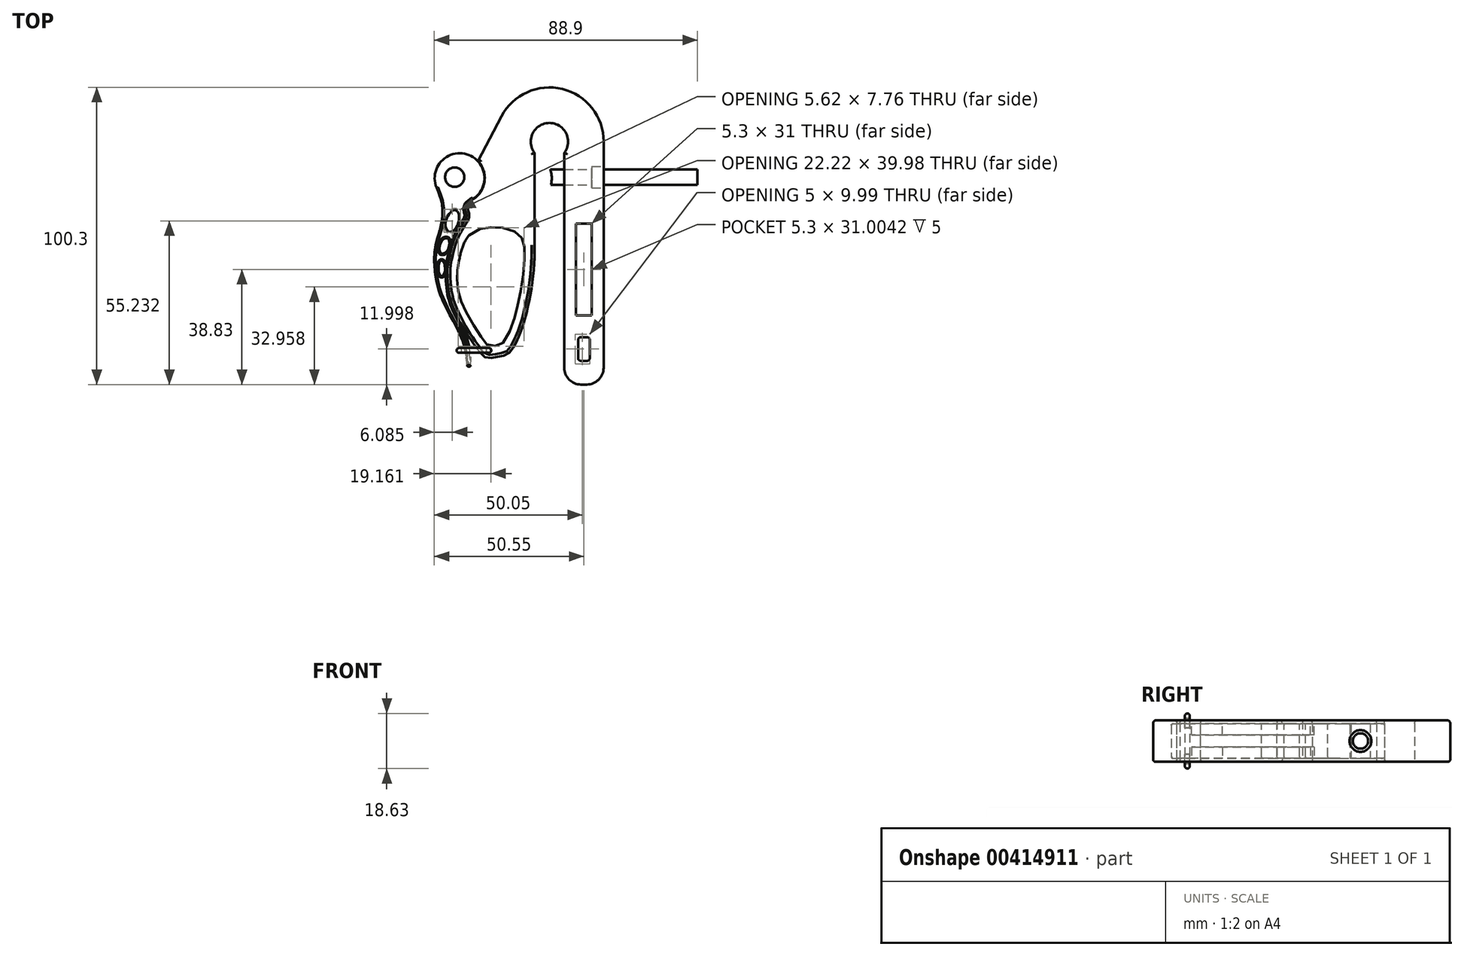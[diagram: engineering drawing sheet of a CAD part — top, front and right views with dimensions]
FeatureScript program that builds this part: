
annotation { "Feature Type Name" : "Feature", "Feature Type Description" : "" }
export const myFeature = defineFeature(function(context is Context, id is Id, definition is map)
    precondition{}
    {
        {
            var Q0;
            Q0=qCreatedBy(makeId("Top.planeOp"),FACE);
            var sketch = newSketch(context, id + "F0", { "sketchPlane" : qUnion([Q0])});
            skLineSegment(sketch, "E0", {"start": v(4.25, 15.7) * mm, "end": v(14.25, 15.7) * mm});
            skSolve(sketch);
        }
        {
            var Q0;
            Q0=qCreatedBy(makeId("Top.planeOp"),FACE);
            var sketch = newSketch(context, id + "F1", { "sketchPlane" : qUnion([Q0])});
            skCircle(sketch, "E1", {"center": v(-9.26, -5.46) * mm, "radius": 3.25 * mm});
            skSolve(sketch);
        }
        {
            var Q0;
            Q0=qCreatedBy(makeId("Top.planeOp"),FACE);
            var sketch = newSketch(context, id + "F2", { "sketchPlane" : qUnion([Q0])});
            skLineSegment(sketch, "E2", {"start": v(-10.3, -5.78) * mm, "end": v(52.53, -5.78) * mm});
            skCircle(sketch, "E3", {"center": v(-7.6, -5.78) * mm, "radius": 8.4 * mm});
            skFitSpline(sketch, "E4", {"points": [v(-15.34, -9.05) * mm, v(-13.72, -13.54) * mm, v(-13.38, -15.5) * mm, v(-13.36, -18.35) * mm, v(-14.1, -22.73) * mm, v(-15.23, -26.6) * mm, v(-15.74, -28.68) * mm, v(-16.08, -31.46) * mm, v(-16.14, -34.4) * mm, v(-15.88, -37.64) * mm, v(-15.5, -39.95) * mm, v(-14.68, -43.49) * mm, v(-13.78, -45.98) * mm, v(-10.97, -51.82) * mm, v(-8.53, -56.37) * mm, v(-7.1, -59.45) * mm, v(-6.08, -62.54) * mm, v(-5.33, -66.95) * mm, v(-5.19, -67.88) * mm, v(-5.05, -69.1) * mm, v(-4.96, -69.3) * mm, v(-4.77, -69.34) * mm, v(-4.09, -69.33) * mm, v(-3.77, -69.02) * mm, v(-3.6, -68.48) * mm, v(-3.65, -67.26) * mm, v(-3.98, -64.6) * mm, v(-4.65, -61.42) * mm, v(-5, -60.18) * mm, v(-5.89, -57.85) * mm, v(-6.72, -56) * mm, v(-8.46, -52.48) * mm, v(-9.55, -50.16) * mm, v(-10.27, -48.37) * mm, v(-10.98, -45.85) * mm, v(-11.43, -43.59) * mm, v(-11.72, -40.7) * mm, v(-11.83, -37.94) * mm, v(-11.8, -36.87) * mm, v(-11.65, -35.17) * mm, v(-11.43, -33.62) * mm, v(-11.1, -32.1) * mm, v(-10.18, -28.54) * mm, v(-9.68, -27) * mm, v(-8.1, -23.55) * mm, v(-6.99, -21.67) * mm, v(-5.8, -19.74) * mm, v(-5.58, -19.3) * mm, v(-5.45, -18.9) * mm, v(-5.4, -18.5) * mm, v(-5.41, -18.12) * mm, v(-5.54, -17.64) * mm, v(-5.72, -17.08) * mm, v(-5.82, -16.42) * mm, v(-5.73, -15.64) * mm, v(-5.6, -15.24) * mm, v(-5.17, -14.43) * mm, v(-4.56, -13.85) * mm, v(-3, -12.81) * mm], "startDerivative": vector(70.6, -181.98) * mm, "endDerivative": vector(100.87, 65.97) * mm});
            skFitSpline(sketch, "E5", {"points": [v(-12.38, -21.6) * mm, v(-12.3, -20.68) * mm, v(-11.9, -19.22) * mm, v(-10.97, -17.7) * mm, v(-10.2, -16.9) * mm, v(-9.44, -16.54) * mm, v(-8.67, -16.63) * mm, v(-8.14, -17.3) * mm, v(-7.79, -18.55) * mm, v(-7.83, -20.2) * mm, v(-8.38, -21.96) * mm, v(-9.3, -23.15) * mm, v(-10.26, -23.86) * mm, v(-10.94, -24) * mm, v(-11.3, -23.86) * mm, v(-11.8, -23.39) * mm, v(-12.2, -22.56) * mm, v(-12.38, -21.6) * mm]});
            skFitSpline(sketch, "E6", {"points": [v(-14.34, -28.7) * mm, v(-14.12, -27.96) * mm, v(-13.63, -27.02) * mm, v(-12.98, -26.32) * mm, v(-12.3, -26.07) * mm, v(-11.62, -26.18) * mm, v(-11.23, -26.62) * mm, v(-11.03, -27.4) * mm, v(-11.15, -28.57) * mm, v(-11.63, -29.94) * mm, v(-12.2, -30.69) * mm, v(-12.9, -31.17) * mm, v(-13.48, -31.26) * mm, v(-13.94, -31.1) * mm, v(-14.28, -30.5) * mm, v(-14.41, -29.7) * mm, v(-14.34, -28.7) * mm]});
            skFitSpline(sketch, "E7", {"points": [v(-14.7, -35.72) * mm, v(-14.54, -34.72) * mm, v(-14.3, -34.12) * mm, v(-13.97, -33.72) * mm, v(-13.5, -33.64) * mm, v(-13.16, -33.88) * mm, v(-12.84, -34.4) * mm, v(-12.6, -35.26) * mm, v(-12.54, -36.12) * mm, v(-12.54, -36.9) * mm, v(-12.72, -37.72) * mm, v(-13.03, -38.4) * mm, v(-13.3, -38.74) * mm, v(-13.7, -38.85) * mm, v(-14.12, -38.56) * mm, v(-14.5, -37.72) * mm, v(-14.68, -36.96) * mm, v(-14.7, -35.72) * mm]});
            skSolve(sketch);
        }
        {
            var Q0;
            {var subQ0=sQuery(id+"F2.wireOp",EDGE,"E4");Q0=makeQuery(id+"F2.imprint","IMPRINT",FACE,{"disambiguationData":[TD([[makeQuery(id+"F2.imprint","IMPRINT",EDGE,{"derivedFrom":subQ0}),1.0]])]});}
            var Q1;
            {var subQ0=sQuery(id+"F2.wireOp",EDGE,"E4");var subQ1=sQuery(id+"F2.wireOp",EDGE,"E3");var subQ2=makeQuery(id+"F2.imprint","INTERSECT",VERTEX,{"disambiguationData":[OD(0.0)],"derivedFrom":[subQ1,subQ0]});Q1=makeQuery(id+"F2.imprint","IMPRINT",FACE,{"disambiguationData":[TD([[makeQuery(id+"F2.imprint","IMPRINT",EDGE,{"disambiguationData":[TD([[subQ2,1.0]])],"derivedFrom":subQ1}),1.0]])]});}
            extrude(context, id + "F3", {"entities" : qUnion([Q0, Q1]), "depth" : 11.64 * mm});
        }
        {
            var Q0;
            Q0=qCreatedBy(makeId("Top.planeOp"),FACE);
            var sketch = newSketch(context, id + "F4", { "sketchPlane" : qUnion([Q0])});
            skCircle(sketch, "E8", {"center": v(-9.26, -5.46) * mm, "radius": 3.25 * mm});
            skSolve(sketch);
        }
        {
            var Q0;
            Q0=makeQuery(id+"F1.imprint","IMPRINT",FACE,{"disambiguationData":[TD([[makeQuery(id+"F1.imprint","IMPRINT",EDGE,{"derivedFrom":sQuery(id+"F1.wireOp",EDGE,"E1")}),1.0]])]});
            extrude(context, id + "F5", {"entities" : qUnion([Q0]), "operationType" : NewBodyOperationType.REMOVE, "endBound" : BoundingType.THROUGH_ALL, "depth" : 25 * mm});
        }
        {
            var Q0;
            Q0=makeQuery(id+"F3.opExtrude","CAP_EDGE",EDGE,{"disambiguationData":[OSD([sQuery(id+"F2.wireOp",EDGE,"E4")])],"isStart":false});
            var Q1;
            Q1=makeQuery(id+"F3.opExtrude","CAP_EDGE",EDGE,{"disambiguationData":[OSD([sQuery(id+"F2.wireOp",EDGE,"E3")])],"isStart":false});
            var Q2;
            Q2=makeQuery(id+"F3.opExtrude","CAP_EDGE",EDGE,{"disambiguationData":[OSD([sQuery(id+"F2.wireOp",EDGE,"E5")])],"isStart":false});
            var Q3;
            Q3=makeQuery(id+"F3.opExtrude","CAP_EDGE",EDGE,{"disambiguationData":[OSD([sQuery(id+"F2.wireOp",EDGE,"E6")])],"isStart":false});
            var Q4;
            Q4=makeQuery(id+"F3.opExtrude","CAP_EDGE",EDGE,{"disambiguationData":[OSD([sQuery(id+"F2.wireOp",EDGE,"E7")])],"isStart":false});
            var Q5;
            Q5=makeQuery(id+"F3.opExtrude","CAP_EDGE",EDGE,{"disambiguationData":[OSD([sQuery(id+"F2.wireOp",EDGE,"E4")])],"isStart":true});
            var Q6;
            Q6=makeQuery(id+"F3.opExtrude","CAP_EDGE",EDGE,{"disambiguationData":[OSD([sQuery(id+"F2.wireOp",EDGE,"E6")])],"isStart":true});
            var Q7;
            Q7=makeQuery(id+"F3.opExtrude","CAP_EDGE",EDGE,{"disambiguationData":[OSD([sQuery(id+"F2.wireOp",EDGE,"E5")])],"isStart":true});
            var Q8;
            Q8=makeQuery(id+"F3.opExtrude","CAP_EDGE",EDGE,{"disambiguationData":[OSD([sQuery(id+"F2.wireOp",EDGE,"E7")])],"isStart":true});
            fillet(context, id + "F6", {"entities" : qUnion([Q0, Q1, Q2, Q3, Q4, Q5, Q6, Q7, Q8]), "radius" : 0.5 * mm, "tangentPropagation" : true, "allowEdgeOverflow" : false});
        }
        {
            var Q0;
            Q0=qCreatedBy(makeId("Top.planeOp"),FACE);
            cPlane(context, id + "F7", {"entities" : qUnion([Q0]), "cplaneType" : CPlaneType.OFFSET, "offset" : 5.83 * mm, "width" : 150 * mm, "height" : 150 * mm});
        }
        {
            var Q0;
            Q0=qCreatedBy(id+"F7.planeOp",FACE);
            var sketch = newSketch(context, id + "F8", { "sketchPlane" : qUnion([Q0])});
            skLineSegment(sketch, "E9", {"start": v(0.79, -5.46) * mm, "end": v(40, -5.46) * mm});
            skLineSegment(sketch, "E10", {"start": v(-9.26, -5.46) * mm, "end": v(10.7, -5.46) * mm, "construction": true});
            skSolve(sketch);
        }
        {
            var Q0;
            Q0=qCreatedBy(makeId("Right.planeOp"),FACE);
            cPlane(context, id + "F9", {"entities" : qUnion([Q0]), "cplaneType" : CPlaneType.OFFSET, "offset" : 50 * mm, "width" : 150 * mm, "height" : 150 * mm});
        }
        {
            var Q0;
            Q0=qCreatedBy(id+"F9.planeOp",FACE);
            var sketch = newSketch(context, id + "F10", { "sketchPlane" : qUnion([Q0])});
            skCircle(sketch, "E11", {"center": v(-5.46, 5.83) * mm, "radius": 2.6 * mm});
            skSolve(sketch);
        }
        {
            var Q0;
            Q0=qSketchRegion(id+"F10",true);
            extrude(context, id + "F11", {"entities" : qUnion([Q0]), "endBound" : BoundingType.UP_TO_NEXT, "oppositeDirection" : true, "depth" : 25 * mm});
        }
        {
            var Q0;
            Q0=makeQuery(id+"F3.opExtrude","SWEPT_BODY",BODY,{"disambiguationData":[OSD([sQuery(id+"F2.wireOp",EDGE,"E3"),sQuery(id+"F2.wireOp",EDGE,"E4"),sQuery(id+"F2.wireOp",EDGE,"E5"),sQuery(id+"F2.wireOp",EDGE,"E6"),sQuery(id+"F2.wireOp",EDGE,"E7")])]});
            var Q1;
            Q1=qCreatedBy(makeId("Right.planeOp"),FACE);
            transform(context, id + "F12", {"entities" : qUnion([Q0]), "transformType" : TransformType.TRANSLATION_DISTANCE, "transformDirection" : qUnion([Q1]), "distance" : 22.75 * mm, "oppositeDirection" : true, "makeCopy" : false});
        }
        {
            var Q0;
            Q0=qCreatedBy(id+"F7.planeOp",FACE);
            var sketch = newSketch(context, id + "F13", { "sketchPlane" : qUnion([Q0])});
            skCircle(sketch, "E12", {"center": v(0, 6.54) * mm, "radius": 6.3 * mm, "construction": true});
            skArc(sketch, "E13", {"start": v(-18.3, 6.54) * mm, "mid": v(0, 24.84) * mm, "end": v(18.3, 6.54) * mm, "construction": true});
            skLineSegment(sketch, "E14", {"start": v(-5, 2.7) * mm, "end": v(-5, -75.46) * mm, "construction": true});
            skLineSegment(sketch, "E15.MirrorCS", {"start": v(5, 2.7) * mm, "end": v(5, -75.46) * mm, "construction": true});
            skLineSegment(sketch, "E16", {"start": v(18.3, 6.54) * mm, "end": v(18.3, -75.46) * mm, "construction": true});
            skLineSegment(sketch, "E17", {"start": v(-24.12, 0) * mm, "end": v(-16.2, 15.06) * mm, "construction": true});
            skArc(sketch, "E18.0", {"start": v(-24.12, 0) * mm, "mid": v(-21.95, -7.05) * mm, "end": v(-26.11, -13.15) * mm, "construction": true});
            skFitSpline(sketch, "E19.0", {"points": [v(-25.7, -12.88) * mm, v(-25.84, -12.97) * mm, v(-26.1, -13.15) * mm, v(-26.5, -13.4) * mm, v(-26.9, -13.67) * mm, v(-27.3, -13.94) * mm, v(-27.6, -14.19) * mm, v(-27.8, -14.42) * mm, v(-27.97, -14.67) * mm, v(-28.12, -14.95) * mm, v(-28.24, -15.24) * mm, v(-28.33, -15.45) * mm, v(-28.4, -15.67) * mm, v(-28.45, -15.97) * mm, v(-28.49, -16.36) * mm, v(-28.45, -16.8) * mm, v(-28.34, -17.18) * mm, v(-28.25, -17.48) * mm, v(-28.17, -17.7) * mm, v(-28.1, -17.94) * mm, v(-28.06, -18.2) * mm, v(-28.06, -18.44) * mm, v(-28.07, -18.68) * mm, v(-28.1, -18.94) * mm, v(-28.18, -19.18) * mm, v(-28.28, -19.4) * mm, v(-28.38, -19.63) * mm, v(-28.5, -19.84) * mm, v(-28.74, -20.25) * mm, v(-29.12, -20.86) * mm, v(-29.63, -21.67) * mm, v(-30.15, -22.48) * mm, v(-30.63, -23.3) * mm, v(-31.05, -24.13) * mm, v(-31.45, -24.98) * mm, v(-31.84, -25.84) * mm, v(-32.2, -26.7) * mm, v(-32.56, -27.57) * mm, v(-32.82, -28.47) * mm, v(-33.07, -29.4) * mm, v(-33.3, -30.31) * mm, v(-33.54, -31.23) * mm, v(-33.77, -32.16) * mm, v(-34, -33.08) * mm, v(-34.16, -34) * mm, v(-34.29, -34.92) * mm, v(-34.38, -35.85) * mm, v(-34.44, -36.63) * mm, v(-34.48, -37.25) * mm, v(-34.5, -37.87) * mm, v(-34.48, -38.65) * mm, v(-34.44, -39.59) * mm, v(-34.4, -40.53) * mm, v(-34.32, -41.47) * mm, v(-34.21, -42.73) * mm, v(-34, -44.28) * mm, v(-33.66, -45.79) * mm, v(-33.35, -46.98) * mm, v(-33.09, -47.87) * mm, v(-32.8, -48.75) * mm, v(-32.44, -49.61) * mm, v(-32.06, -50.47) * mm, v(-31.67, -51.32) * mm, v(-31.26, -52.17) * mm, v(-30.84, -53.01) * mm, v(-30.43, -53.85) * mm, v(-30, -54.7) * mm, v(-29.59, -55.54) * mm, v(-29.17, -56.4) * mm, v(-28.78, -57.25) * mm, v(-28.42, -58.13) * mm, v(-28.08, -59) * mm, v(-27.8, -59.74) * mm, v(-27.6, -60.34) * mm, v(-27.46, -60.8) * mm, v(-27.34, -61.25) * mm, v(-27.2, -61.87) * mm, v(-27.02, -62.64) * mm, v(-26.82, -63.56) * mm, v(-26.64, -64.5) * mm, v(-26.5, -65.43) * mm, v(-26.41, -66.22) * mm, v(-26.35, -66.84) * mm, v(-26.3, -67.31) * mm, v(-26.26, -67.7) * mm, v(-26.24, -68.02) * mm, v(-26.23, -68.27) * mm, v(-26.25, -68.51) * mm, v(-26.3, -68.76) * mm, v(-26.4, -69) * mm, v(-26.48, -69.14) * mm, v(-26.54, -69.21) * mm], "construction": true});
            skFitSpline(sketch, "E20", {"points": [v(-29.53, -55.65) * mm, v(-24.4, -63.35) * mm, v(-21.24, -66.37) * mm, v(-16.84, -65.96) * mm, v(-13.48, -64.6) * mm, v(-5.01, -28.32) * mm], "startDerivative": vector(26.21, -45.22) * mm, "endDerivative": vector(-2.06, 128.2) * mm, "construction": true});
            skLineSegment(sketch, "E21", {"start": v(5, -75.46) * mm, "end": v(18.3, -75.46) * mm, "construction": true});
            skFitSpline(sketch, "E22", {"points": [v(-30.52, -33.64) * mm, v(-27.1, -25.02) * mm], "startDerivative": vector(2.2, 9.83) * mm, "endDerivative": vector(6.97, 8.55) * mm});
            skFitSpline(sketch, "E23", {"points": [v(-29.66, -21.72) * mm, v(-31.4, -24.89) * mm, v(-32.64, -27.88) * mm, v(-33.72, -31.93) * mm], "startDerivative": vector(-6, -10.28) * mm, "endDerivative": vector(-2.9, -11.97) * mm});
            skLineSegment(sketch, "E24", {"start": v(-16.2, 15.06) * mm, "end": v(-24.12, 0) * mm});
            skArc(sketch, "E25", {"start": v(-16.2, 15.06) * mm, "mid": v(4.39, 24.3) * mm, "end": v(18.3, 6.54) * mm});
            skLineSegment(sketch, "E26", {"start": v(18.3, -75.46) * mm, "end": v(18.3, 6.54) * mm});
            skLineSegment(sketch, "E27", {"start": v(18.3, -75.46) * mm, "end": v(5, -75.46) * mm});
            skLineSegment(sketch, "E28", {"start": v(5, 2.7) * mm, "end": v(5, -75.46) * mm});
            skArc(sketch, "E29", {"start": v(5, 2.7) * mm, "mid": v(0, 12.84) * mm, "end": v(-5, 2.7) * mm});
            skLineSegment(sketch, "E30", {"start": v(-5, -28.36) * mm, "end": v(-5, 2.7) * mm});
            skArc(sketch, "E31", {"start": v(-24.12, 0) * mm, "mid": v(-21.95, -7.05) * mm, "end": v(-26.11, -13.15) * mm});
            skFitSpline(sketch, "E32", {"points": [v(-26.11, -13.15) * mm, v(-27.43, -14.05) * mm, v(-28.24, -15.23) * mm, v(-28.47, -16.48) * mm, v(-28.17, -17.73) * mm, v(-28.08, -18.75) * mm, v(-28.41, -19.68) * mm, v(-29, -20.66) * mm, v(-29.66, -21.72) * mm, v(-31, -24.11) * mm, v(-32.48, -27.4) * mm, v(-33.37, -30.51) * mm, v(-33.72, -31.93) * mm, v(-34.21, -34.4) * mm, v(-34.48, -37.3) * mm, v(-34.42, -39.9) * mm, v(-34.2, -42.74) * mm, v(-33.72, -45.52) * mm, v(-32.98, -48.18) * mm, v(-31.97, -50.66) * mm, v(-30.75, -53.2) * mm, v(-29.53, -55.65) * mm, v(-28.06, -58.07) * mm, v(-26.11, -60.95) * mm, v(-24.4, -63.35) * mm, v(-22.5, -65.67) * mm, v(-21.24, -66.37) * mm, v(-18.98, -66.37) * mm, v(-16.84, -65.96) * mm, v(-15.68, -65.77) * mm, v(-13.48, -64.6) * mm, v(-9.9, -58.13) * mm, v(-8.06, -52.52) * mm, v(-6.1, -43.39) * mm, v(-5.34, -37.24) * mm, v(-5.07, -33.03) * mm, v(-5, -28.36) * mm], "startDerivative": vector(-67.28, -39.35) * mm, "endDerivative": vector(1.05, 140.54) * mm});
            skFitSpline(sketch, "E33", {"points": [v(-30.52, -33.64) * mm, v(-31.05, -36.67) * mm, v(-31.2, -39.39) * mm, v(-30.86, -43.33) * mm, v(-29.86, -47.04) * mm, v(-28.05, -51.13) * mm, v(-24.49, -57.22) * mm, v(-21.97, -60.98) * mm, v(-20.5, -62.36) * mm, v(-17.88, -62.31) * mm, v(-15.64, -61.36) * mm, v(-12.79, -56.03) * mm, v(-11.12, -50.32) * mm, v(-9.79, -44.62) * mm, v(-8.6, -35.77) * mm, v(-8.41, -30.11) * mm, v(-9.03, -26.64) * mm, v(-10.4, -24.74) * mm, v(-14.21, -22.93) * mm, v(-19.02, -22.36) * mm, v(-22.87, -22.79) * mm, v(-27.1, -25.02) * mm], "startDerivative": vector(-14.95, -76.87) * mm, "endDerivative": vector(-98.96, -93.3) * mm});
            skSolve(sketch);
        }
        {
            var Q0;
            Q0=makeQuery(id+"F13.imprint","IMPRINT",FACE,{"disambiguationData":[TD([[makeQuery(id+"F13.imprint","IMPRINT",EDGE,{"derivedFrom":sQuery(id+"F13.wireOp",EDGE,"E22")}),1.0]])]});
            extrude(context, id + "F14", {"entities" : qUnion([Q0]), "endBound" : BoundingType.SYMMETRIC, "depth" : 14 * mm});
        }
        {
            var Q0;
            Q0=makeQuery(id+"F3.opExtrude","SWEPT_BODY",BODY,{"disambiguationData":[OSD([sQuery(id+"F2.wireOp",EDGE,"E3"),sQuery(id+"F2.wireOp",EDGE,"E4"),sQuery(id+"F2.wireOp",EDGE,"E5"),sQuery(id+"F2.wireOp",EDGE,"E6"),sQuery(id+"F2.wireOp",EDGE,"E7")])]});
            var Q1;
            Q1=makeQuery(id+"F14.opExtrude","SWEPT_BODY",BODY,{"disambiguationData":[OSD([sQuery(id+"F13.wireOp",EDGE,"E23"),sQuery(id+"F13.wireOp",EDGE,"E24"),sQuery(id+"F13.wireOp",EDGE,"E25"),sQuery(id+"F13.wireOp",EDGE,"E26"),sQuery(id+"F13.wireOp",EDGE,"E27"),sQuery(id+"F13.wireOp",EDGE,"E28"),sQuery(id+"F13.wireOp",EDGE,"E29"),sQuery(id+"F13.wireOp",EDGE,"E30"),sQuery(id+"F13.wireOp",EDGE,"E31"),sQuery(id+"F13.wireOp",EDGE,"E32")])]});
            booleanBodies(context, id + "F15", {"operationType" : BooleanOperationType.SUBTRACTION, "tools" : qUnion([Q0]), "targets" : qUnion([Q1]), "keepTools" : true});
        }
        {
            var Q0;
            Q0=makeQuery(id+"F14.opExtrude","CAP_FACE",FACE,{"disambiguationData":[OSD([sQuery(id+"F13.wireOp",EDGE,"E23"),sQuery(id+"F13.wireOp",EDGE,"E24"),sQuery(id+"F13.wireOp",EDGE,"E25"),sQuery(id+"F13.wireOp",EDGE,"E26"),sQuery(id+"F13.wireOp",EDGE,"E27"),sQuery(id+"F13.wireOp",EDGE,"E28"),sQuery(id+"F13.wireOp",EDGE,"E29"),sQuery(id+"F13.wireOp",EDGE,"E30"),sQuery(id+"F13.wireOp",EDGE,"E31"),sQuery(id+"F13.wireOp",EDGE,"E32")])],"isStart":false});
            var sketch = newSketch(context, id + "F16", { "sketchPlane" : qUnion([Q0])});
            skLineSegment(sketch, "E34.0", {"start": v(9, -21.13) * mm, "end": v(9, -52.13) * mm});
            skLineSegment(sketch, "E35.0", {"start": v(14.3, -52.13) * mm, "end": v(14.3, -21.13) * mm});
            skLineSegment(sketch, "E36", {"start": v(9, -21.13) * mm, "end": v(14.3, -21.13) * mm});
            skLineSegment(sketch, "E37", {"start": v(9, -52.13) * mm, "end": v(14.3, -52.13) * mm});
            skSolve(sketch);
        }
        {
            var Q0;
            Q0=makeQuery(id+"F16.imprint","IMPRINT",FACE,{"disambiguationData":[TD([[makeQuery(id+"F16.imprint","IMPRINT",EDGE,{"derivedFrom":sQuery(id+"F16.wireOp",EDGE,"E34.0")}),1.0]])]});
            extrude(context, id + "F17", {"entities" : qUnion([Q0]), "operationType" : NewBodyOperationType.REMOVE, "oppositeDirection" : true, "depth" : 5 * mm});
        }
        {
            var Q0;
            Q0=makeQuery(id+"F14.opExtrude","CAP_FACE",FACE,{"disambiguationData":[OSD([sQuery(id+"F13.wireOp",EDGE,"E23"),sQuery(id+"F13.wireOp",EDGE,"E24"),sQuery(id+"F13.wireOp",EDGE,"E25"),sQuery(id+"F13.wireOp",EDGE,"E26"),sQuery(id+"F13.wireOp",EDGE,"E27"),sQuery(id+"F13.wireOp",EDGE,"E28"),sQuery(id+"F13.wireOp",EDGE,"E29"),sQuery(id+"F13.wireOp",EDGE,"E30"),sQuery(id+"F13.wireOp",EDGE,"E31"),sQuery(id+"F13.wireOp",EDGE,"E32")])],"isStart":true});
            var sketch = newSketch(context, id + "F18", { "sketchPlane" : qUnion([Q0])});
            skLineSegment(sketch, "E38.0", {"start": v(9, 21.13) * mm, "end": v(9, 52.13) * mm});
            skLineSegment(sketch, "E39.0", {"start": v(14.3, 52.13) * mm, "end": v(14.3, 21.13) * mm});
            skLineSegment(sketch, "E40", {"start": v(9, 52.13) * mm, "end": v(14.3, 52.13) * mm});
            skLineSegment(sketch, "E41", {"start": v(9, 21.13) * mm, "end": v(14.3, 21.13) * mm});
            skSolve(sketch);
        }
        {
            var Q0;
            Q0=makeQuery(id+"F18.imprint","IMPRINT",FACE,{"disambiguationData":[TD([[makeQuery(id+"F18.imprint","IMPRINT",EDGE,{"derivedFrom":sQuery(id+"F18.wireOp",EDGE,"E38.0")}),-1.0]])]});
            extrude(context, id + "F19", {"entities" : qUnion([Q0]), "operationType" : NewBodyOperationType.REMOVE, "oppositeDirection" : true, "depth" : 5 * mm});
        }
        {
            var Q0;
            Q0=makeQuery(id+"F14.opExtrude","SWEPT_FACE",FACE,{"disambiguationData":[OSD([sQuery(id+"F13.wireOp",EDGE,"E26")])]});
            var sketch = newSketch(context, id + "F20", { "sketchPlane" : qUnion([Q0])});
            skCircle(sketch, "E42", {"center": v(-5.46, 5.83) * mm, "radius": 3.67 * mm});
            skSolve(sketch);
        }
        {
            var Q0;
            Q0=qSketchRegion(id+"F20",true);
            extrude(context, id + "F21", {"entities" : qUnion([Q0]), "operationType" : NewBodyOperationType.REMOVE, "oppositeDirection" : true, "depth" : 4 * mm});
        }
        {
            var Q0;
            Q0=makeQuery(id+"F16.imprint","IMPRINT",FACE,{"disambiguationData":[TD([[makeQuery(id+"F16.imprint","IMPRINT",EDGE,{"derivedFrom":sQuery(id+"F16.wireOp",EDGE,"E34.0")}),-1.0]])]});
            var sketch = newSketch(context, id + "F22", { "sketchPlane" : qUnion([Q0])});
            skLineSegment(sketch, "E43.bottom", {"start": v(9.65, -59.46) * mm, "end": v(13.65, -59.46) * mm});
            skLineSegment(sketch, "E43.top", {"start": v(9.65, -67.46) * mm, "end": v(13.65, -67.46) * mm});
            skLineSegment(sketch, "E43.left", {"start": v(9.65, -59.46) * mm, "end": v(9.65, -67.46) * mm});
            skLineSegment(sketch, "E43.right", {"start": v(13.65, -59.46) * mm, "end": v(13.65, -67.46) * mm});
            skPoint(sketch, "E43.middle", {"position": v(11.65, -63.46) * mm});
            skSolve(sketch);
        }
        {
            var Q0;
            Q0=qSketchRegion(id+"F22",true);
            extrude(context, id + "F23", {"entities" : qUnion([Q0]), "operationType" : NewBodyOperationType.REMOVE, "endBound" : BoundingType.THROUGH_ALL, "oppositeDirection" : true, "depth" : 25 * mm});
        }
        {
            var Q0;
            Q0=makeQuery(id+"F23.boolean.opBoolean","COPY",EDGE,{"derivedFrom":makeQuery(id+"F23.opExtrude","SWEPT_EDGE",EDGE,{"disambiguationData":[OSD([sQuery(id+"F22.wireOp",EDGE,"E43.bottom"),sQuery(id+"F22.wireOp",EDGE,"E43.right")])]})});
            var Q1;
            Q1=makeQuery(id+"F23.boolean.opBoolean","COPY",EDGE,{"derivedFrom":makeQuery(id+"F23.opExtrude","SWEPT_EDGE",EDGE,{"disambiguationData":[OSD([sQuery(id+"F22.wireOp",EDGE,"E43.top"),sQuery(id+"F22.wireOp",EDGE,"E43.right")])]})});
            var Q2;
            Q2=makeQuery(id+"F23.boolean.opBoolean","COPY",FACE,{"derivedFrom":makeQuery(id+"F23.opExtrude","SWEPT_FACE",FACE,{"disambiguationData":[OSD([sQuery(id+"F22.wireOp",EDGE,"E43.left")])]})});
            fillet(context, id + "F24", {"entities" : qUnion([Q0, Q1, Q2]), "radius" : 1 * mm, "tangentPropagation" : true, "allowEdgeOverflow" : false});
        }
        {
            var Q0;
            Q0=makeQuery(id+"F14.opExtrude","SWEPT_EDGE",EDGE,{"disambiguationData":[OSD([sQuery(id+"F13.wireOp",EDGE,"E27"),sQuery(id+"F13.wireOp",EDGE,"E28")])]});
            var Q1;
            Q1=makeQuery(id+"F14.opExtrude","SWEPT_EDGE",EDGE,{"disambiguationData":[OSD([sQuery(id+"F13.wireOp",EDGE,"E26"),sQuery(id+"F13.wireOp",EDGE,"E27")])]});
            fillet(context, id + "F25", {"entities" : qUnion([Q0, Q1]), "radius" : 5.65 * mm, "tangentPropagation" : true, "allowEdgeOverflow" : false});
        }
        {
            var Q0;
            Q0=makeQuery(id+"F14.opExtrude","CAP_EDGE",EDGE,{"disambiguationData":[OSD([sQuery(id+"F13.wireOp",EDGE,"E24")])],"isStart":false});
            var Q1;
            Q1=makeQuery(id+"F14.opExtrude","CAP_EDGE",EDGE,{"disambiguationData":[OSD([sQuery(id+"F13.wireOp",EDGE,"E25")])],"isStart":false});
            var Q2;
            Q2=makeQuery(id+"F14.opExtrude","CAP_EDGE",EDGE,{"disambiguationData":[OSD([sQuery(id+"F13.wireOp",EDGE,"E26")])],"isStart":false});
            var Q3;
            {var subQ0=sQuery(id+"F13.wireOp",EDGE,"E32");Q3=makeQuery(id+"F14.opExtrude","CAP_EDGE",EDGE,{"disambiguationData":[OSD([subQ0]),TDD([makeQuery(id+"F13.imprint","IMPRINT",EDGE,{"disambiguationData":[TD([[makeQuery(id+"F13.imprint","INTERSECT",VERTEX,{"disambiguationData":[OD(1.0)],"derivedFrom":[sQuery(id+"F13.wireOp",EDGE,"E23"),subQ0]}),-1.0]])],"derivedFrom":subQ0})])],"isStart":false});}
            var Q4;
            Q4=makeQuery(id+"F14.opExtrude","CAP_EDGE",EDGE,{"disambiguationData":[OSD([sQuery(id+"F13.wireOp",EDGE,"E30")])],"isStart":false});
            var Q5;
            Q5=makeQuery(id+"F14.opExtrude","CAP_EDGE",EDGE,{"disambiguationData":[OSD([sQuery(id+"F13.wireOp",EDGE,"E28")])],"isStart":false});
            var Q6;
            Q6=makeQuery(id+"F14.opExtrude","CAP_EDGE",EDGE,{"disambiguationData":[OSD([sQuery(id+"F13.wireOp",EDGE,"E29")])],"isStart":false});
            var Q7;
            Q7=makeQuery(id+"F14.opExtrude","CAP_EDGE",EDGE,{"disambiguationData":[OSD([sQuery(id+"F13.wireOp",EDGE,"E31")])],"isStart":false});
            var Q8;
            {var subQ0=sQuery(id+"F13.wireOp",EDGE,"E32");Q8=makeQuery(id+"F14.opExtrude","CAP_EDGE",EDGE,{"disambiguationData":[OSD([subQ0]),TDD([makeQuery(id+"F13.imprint","IMPRINT",EDGE,{"disambiguationData":[TD([[makeQuery(id+"F13.imprint","INTERSECT",VERTEX,{"disambiguationData":[OD(0.0)],"derivedFrom":[sQuery(id+"F13.wireOp",EDGE,"E23"),subQ0]}),1.0]])],"derivedFrom":subQ0})])],"isStart":false});}
            var Q9;
            {var subQ0=sQuery(id+"F13.wireOp",EDGE,"E32");var subQ1=sQuery(id+"F13.wireOp",EDGE,"E23");Q9=makeQuery(id+"F14.opExtrude","CAP_EDGE",EDGE,{"disambiguationData":[OSD([subQ0]),TDD([makeQuery(id+"F13.imprint","IMPRINT",EDGE,{"disambiguationData":[TD([[makeQuery(id+"F13.imprint","INTERSECT",VERTEX,{"disambiguationData":[OD(2.0)],"derivedFrom":[subQ1,subQ0]}),-1.0]])],"derivedFrom":subQ0})])],"isStart":false});}
            var Q10;
            {var subQ0=sQuery(id+"F13.wireOp",EDGE,"E32");var subQ1=sQuery(id+"F13.wireOp",EDGE,"E23");Q10=makeQuery(id+"F14.opExtrude","CAP_EDGE",EDGE,{"disambiguationData":[OSD([subQ1]),TDD([makeQuery(id+"F13.imprint","IMPRINT",EDGE,{"disambiguationData":[TD([[makeQuery(id+"F13.imprint","INTERSECT",VERTEX,{"disambiguationData":[OD(0.0)],"derivedFrom":[subQ1,subQ0]}),-1.0]])],"derivedFrom":subQ1})])],"isStart":false});}
            var Q11;
            {var subQ0=sQuery(id+"F13.wireOp",EDGE,"E32");var subQ1=sQuery(id+"F13.wireOp",EDGE,"E23");Q11=makeQuery(id+"F14.opExtrude","CAP_EDGE",EDGE,{"disambiguationData":[OSD([subQ1]),TDD([makeQuery(id+"F13.imprint","IMPRINT",EDGE,{"disambiguationData":[TD([[makeQuery(id+"F13.imprint","INTERSECT",VERTEX,{"disambiguationData":[OD(1.0)],"derivedFrom":[subQ1,subQ0]}),1.0]])],"derivedFrom":subQ1})])],"isStart":false});}
            fillet(context, id + "F26", {"entities" : qUnion([Q0, Q1, Q2, Q3, Q4, Q5, Q6, Q7, Q8, Q9, Q10, Q11]), "radius" : 1 * mm, "tangentPropagation" : true, "allowEdgeOverflow" : false});
        }
        {
            var Q0;
            Q0=makeQuery(id+"F14.opExtrude","CAP_EDGE",EDGE,{"disambiguationData":[OSD([sQuery(id+"F13.wireOp",EDGE,"E25")])],"isStart":true});
            var Q1;
            Q1=makeQuery(id+"F14.opExtrude","CAP_EDGE",EDGE,{"disambiguationData":[OSD([sQuery(id+"F13.wireOp",EDGE,"E24")])],"isStart":true});
            var Q2;
            Q2=makeQuery(id+"F14.opExtrude","CAP_EDGE",EDGE,{"disambiguationData":[OSD([sQuery(id+"F13.wireOp",EDGE,"E31")])],"isStart":true});
            var Q3;
            {var subQ0=sQuery(id+"F13.wireOp",EDGE,"E32");Q3=makeQuery(id+"F14.opExtrude","CAP_EDGE",EDGE,{"disambiguationData":[OSD([subQ0]),TDD([makeQuery(id+"F13.imprint","IMPRINT",EDGE,{"disambiguationData":[TD([[makeQuery(id+"F13.imprint","INTERSECT",VERTEX,{"disambiguationData":[OD(0.0)],"derivedFrom":[sQuery(id+"F13.wireOp",EDGE,"E23"),subQ0]}),1.0]])],"derivedFrom":subQ0})])],"isStart":true});}
            var Q4;
            {var subQ0=sQuery(id+"F13.wireOp",EDGE,"E32");var subQ1=sQuery(id+"F13.wireOp",EDGE,"E23");Q4=makeQuery(id+"F14.opExtrude","CAP_EDGE",EDGE,{"disambiguationData":[OSD([subQ0]),TDD([makeQuery(id+"F13.imprint","IMPRINT",EDGE,{"disambiguationData":[TD([[makeQuery(id+"F13.imprint","INTERSECT",VERTEX,{"disambiguationData":[OD(2.0)],"derivedFrom":[subQ1,subQ0]}),-1.0]])],"derivedFrom":subQ0})])],"isStart":true});}
            var Q5;
            {var subQ0=sQuery(id+"F13.wireOp",EDGE,"E32");var subQ1=sQuery(id+"F13.wireOp",EDGE,"E23");Q5=makeQuery(id+"F14.opExtrude","CAP_EDGE",EDGE,{"disambiguationData":[OSD([subQ1]),TDD([makeQuery(id+"F13.imprint","IMPRINT",EDGE,{"disambiguationData":[TD([[makeQuery(id+"F13.imprint","INTERSECT",VERTEX,{"disambiguationData":[OD(0.0)],"derivedFrom":[subQ1,subQ0]}),-1.0]])],"derivedFrom":subQ1})])],"isStart":true});}
            var Q6;
            {var subQ0=sQuery(id+"F13.wireOp",EDGE,"E32");var subQ1=sQuery(id+"F13.wireOp",EDGE,"E23");Q6=makeQuery(id+"F14.opExtrude","CAP_EDGE",EDGE,{"disambiguationData":[OSD([subQ1]),TDD([makeQuery(id+"F13.imprint","IMPRINT",EDGE,{"disambiguationData":[TD([[makeQuery(id+"F13.imprint","INTERSECT",VERTEX,{"disambiguationData":[OD(1.0)],"derivedFrom":[subQ1,subQ0]}),1.0]])],"derivedFrom":subQ1})])],"isStart":true});}
            var Q7;
            {var subQ0=sQuery(id+"F13.wireOp",EDGE,"E32");Q7=makeQuery(id+"F14.opExtrude","CAP_EDGE",EDGE,{"disambiguationData":[OSD([subQ0]),TDD([makeQuery(id+"F13.imprint","IMPRINT",EDGE,{"disambiguationData":[TD([[makeQuery(id+"F13.imprint","INTERSECT",VERTEX,{"disambiguationData":[OD(1.0)],"derivedFrom":[sQuery(id+"F13.wireOp",EDGE,"E23"),subQ0]}),-1.0]])],"derivedFrom":subQ0})])],"isStart":true});}
            var Q8;
            Q8=makeQuery(id+"F14.opExtrude","CAP_EDGE",EDGE,{"disambiguationData":[OSD([sQuery(id+"F13.wireOp",EDGE,"E30")])],"isStart":true});
            var Q9;
            Q9=makeQuery(id+"F14.opExtrude","CAP_EDGE",EDGE,{"disambiguationData":[OSD([sQuery(id+"F13.wireOp",EDGE,"E28")])],"isStart":true});
            var Q10;
            Q10=makeQuery(id+"F14.opExtrude","CAP_EDGE",EDGE,{"disambiguationData":[OSD([sQuery(id+"F13.wireOp",EDGE,"E26")])],"isStart":true});
            var Q11;
            {var subQ0=sQuery(id+"F13.wireOp",EDGE,"E28");var subQ1=sQuery(id+"F13.wireOp",EDGE,"E27");Q11=makeQuery(id+"F25.opFillet","BLEND_EDGE",EDGE,{"blendedFrom":[makeQuery(id+"F14.opExtrude","SWEPT_EDGE",EDGE,{"disambiguationData":[OSD([subQ1,subQ0])]}),makeQuery(id+"F14.opExtrude","CAP_FACE",FACE,{"disambiguationData":[OSD([sQuery(id+"F13.wireOp",EDGE,"E23"),sQuery(id+"F13.wireOp",EDGE,"E24"),sQuery(id+"F13.wireOp",EDGE,"E25"),sQuery(id+"F13.wireOp",EDGE,"E26"),subQ1,subQ0,sQuery(id+"F13.wireOp",EDGE,"E29"),sQuery(id+"F13.wireOp",EDGE,"E30"),sQuery(id+"F13.wireOp",EDGE,"E31"),sQuery(id+"F13.wireOp",EDGE,"E32")])],"isStart":true})],"blendedInto":[makeQuery(id+"F14.opExtrude","CAP_FACE",FACE,{"disambiguationData":[OSD([sQuery(id+"F13.wireOp",EDGE,"E23"),sQuery(id+"F13.wireOp",EDGE,"E24"),sQuery(id+"F13.wireOp",EDGE,"E25"),sQuery(id+"F13.wireOp",EDGE,"E26"),subQ1,subQ0,sQuery(id+"F13.wireOp",EDGE,"E29"),sQuery(id+"F13.wireOp",EDGE,"E30"),sQuery(id+"F13.wireOp",EDGE,"E31"),sQuery(id+"F13.wireOp",EDGE,"E32")])],"isStart":true})]});}
            var Q12;
            {var subQ0=sQuery(id+"F13.wireOp",EDGE,"E27");var subQ1=sQuery(id+"F13.wireOp",EDGE,"E26");Q12=makeQuery(id+"F25.opFillet","BLEND_EDGE",EDGE,{"blendedFrom":[makeQuery(id+"F14.opExtrude","SWEPT_EDGE",EDGE,{"disambiguationData":[OSD([subQ1,subQ0])]}),makeQuery(id+"F14.opExtrude","CAP_FACE",FACE,{"disambiguationData":[OSD([sQuery(id+"F13.wireOp",EDGE,"E23"),sQuery(id+"F13.wireOp",EDGE,"E24"),sQuery(id+"F13.wireOp",EDGE,"E25"),subQ1,subQ0,sQuery(id+"F13.wireOp",EDGE,"E28"),sQuery(id+"F13.wireOp",EDGE,"E29"),sQuery(id+"F13.wireOp",EDGE,"E30"),sQuery(id+"F13.wireOp",EDGE,"E31"),sQuery(id+"F13.wireOp",EDGE,"E32")])],"isStart":true})],"blendedInto":[makeQuery(id+"F14.opExtrude","CAP_FACE",FACE,{"disambiguationData":[OSD([sQuery(id+"F13.wireOp",EDGE,"E23"),sQuery(id+"F13.wireOp",EDGE,"E24"),sQuery(id+"F13.wireOp",EDGE,"E25"),subQ1,subQ0,sQuery(id+"F13.wireOp",EDGE,"E28"),sQuery(id+"F13.wireOp",EDGE,"E29"),sQuery(id+"F13.wireOp",EDGE,"E30"),sQuery(id+"F13.wireOp",EDGE,"E31"),sQuery(id+"F13.wireOp",EDGE,"E32")])],"isStart":true})]});}
            var Q13;
            Q13=makeQuery(id+"F14.opExtrude","CAP_EDGE",EDGE,{"disambiguationData":[OSD([sQuery(id+"F13.wireOp",EDGE,"E27")])],"isStart":true});
            fillet(context, id + "F27", {"entities" : qUnion([Q0, Q1, Q2, Q3, Q4, Q5, Q6, Q7, Q8, Q9, Q10, Q11, Q12, Q13]), "radius" : 0.75 * mm, "tangentPropagation" : true, "allowEdgeOverflow" : false});
        }
        {
            var Q0;
            Q0=makeQuery(id+"F13.imprint","IMPRINT",FACE,{"disambiguationData":[TD([[makeQuery(id+"F13.imprint","IMPRINT",EDGE,{"derivedFrom":sQuery(id+"F13.wireOp",EDGE,"E22")}),-1.0]])]});
            extrude(context, id + "F28", {"entities" : qUnion([Q0]), "operationType" : NewBodyOperationType.ADD, "endBound" : BoundingType.SYMMETRIC, "depth" : 4 * mm});
        }
        {
            var Q0;
            Q0=makeQuery(id+"F16.imprint","IMPRINT",FACE,{"disambiguationData":[TD([[makeQuery(id+"F16.imprint","IMPRINT",EDGE,{"derivedFrom":makeQuery(id+"F14.opExtrude","CAP_EDGE",EDGE,{"disambiguationData":[OSD([sQuery(id+"F13.wireOp",EDGE,"E22")])],"isStart":false})}),-1.0]])]});
            var sketch = newSketch(context, id + "F29", { "sketchPlane" : qUnion([Q0])});
            skCircle(sketch, "E44", {"center": v(-20.54, -63.93) * mm, "radius": 9.19 * mm});
            skCircle(sketch, "E45", {"center": v(-20.54, -63.93) * mm, "radius": 0.81 * mm});
            skSolve(sketch);
        }
        {
            var Q0;
            Q0=makeQuery(id+"F16.imprint","IMPRINT",FACE,{"disambiguationData":[TD([[makeQuery(id+"F16.imprint","IMPRINT",EDGE,{"derivedFrom":sQuery(id+"F16.wireOp",EDGE,"E34.0")}),-1.0]])]});
            var sketch = newSketch(context, id + "F30", { "sketchPlane" : qUnion([Q0])});
            skCircle(sketch, "E46", {"center": v(-20.54, -63.93) * mm, "radius": 0.9 * mm});
            skSolve(sketch);
        }
        {
            var Q0;
            Q0 = qSketchRegion(id + "F30", true);
            extrude(context, id + "F31", {"entities" : qUnion([Q0]), "operationType" : NewBodyOperationType.REMOVE, "oppositeDirection" : true, "depth" : 2.5 * mm});
        }
        {
            var Q0;
            Q0=qCreatedBy(makeId("Front.planeOp"),FACE);
            cPlane(context, id + "F32", {"entities" : qUnion([Q0]), "cplaneType" : CPlaneType.OFFSET, "offset" : 63.93 * mm, "width" : 150 * mm, "height" : 150 * mm});
        }
        {
            var Q0;
            Q0=qCreatedBy(id+"F32.planeOp",FACE);
            var sketch = newSketch(context, id + "F33", { "sketchPlane" : qUnion([Q0])});
            skLineSegment(sketch, "E47", {"start": v(-22.04, 16.35) * mm, "end": v(-22.04, -5.39) * mm, "construction": true});
            skLineSegment(sketch, "E48", {"start": v(-20.54, 12.82) * mm, "end": v(-20.54, 10.32) * mm});
            skLineSegment(sketch, "E49", {"start": v(-17.56, 5.83) * mm, "end": v(-41.1, 5.82) * mm, "construction": true});
            skArc(sketch, "E50", {"start": v(-20.54, 12.82) * mm, "mid": v(-20.98, 13.89) * mm, "end": v(-22.04, 14.32) * mm});
            skLineSegment(sketch, "E51", {"start": v(-22.04, 14.32) * mm, "end": v(-29.04, 14.32) * mm});
            skArc(sketch, "E52", {"start": v(-29.04, 14.32) * mm, "mid": v(-30.08, 13.9) * mm, "end": v(-30.54, 12.88) * mm});
            skLineSegment(sketch, "E53", {"start": v(-30.54, 12.88) * mm, "end": v(-30.54, 5.83) * mm});
            skLineSegment(sketch, "E54.MirrorCS", {"start": v(-30.54, -1.23) * mm, "end": v(-30.54, 5.83) * mm});
            skArc(sketch, "E55.MirrorCS", {"start": v(-29.04, -2.67) * mm, "mid": v(-30.08, -2.26) * mm, "end": v(-30.54, -1.23) * mm});
            skLineSegment(sketch, "E56.MirrorCS", {"start": v(-22.04, -2.67) * mm, "end": v(-29.04, -2.67) * mm});
            skArc(sketch, "E57.MirrorCS", {"start": v(-20.54, -1.17) * mm, "mid": v(-20.98, -2.24) * mm, "end": v(-22.04, -2.67) * mm});
            skLineSegment(sketch, "E58.MirrorCS", {"start": v(-20.54, -1.17) * mm, "end": v(-20.54, 1.33) * mm});
            skSolve(sketch);
        }
        {
            var Q0;
            Q0=makeQuery(id+"F16.imprint","IMPRINT",FACE,{"disambiguationData":[TD([[makeQuery(id+"F16.imprint","IMPRINT",EDGE,{"derivedFrom":sQuery(id+"F16.wireOp",EDGE,"E34.0")}),-1.0]])]});
            var sketch = newSketch(context, id + "F34", { "sketchPlane" : qUnion([Q0])});
            skCircle(sketch, "E59", {"center": v(-20.54, -63.93) * mm, "radius": 0.81 * mm});
            skSolve(sketch);
        }
        {
            var Q0;
            Q0=makeQuery(id+"F34.imprint","IMPRINT",FACE,{"disambiguationData":[TD([[makeQuery(id+"F34.imprint","IMPRINT",EDGE,{"derivedFrom":sQuery(id+"F34.wireOp",EDGE,"E59")}),1.0]])]});
            cPlane(context, id + "F35", {"entities" : qUnion([Q0]), "cplaneType" : CPlaneType.OFFSET, "offset" : 2.5 * mm, "oppositeDirection" : true, "width" : 150 * mm, "height" : 150 * mm});
        }
        {
            var Q0;
            Q0=qCreatedBy(id+"F35.planeOp",FACE);
            var sketch = newSketch(context, id + "F36", { "sketchPlane" : qUnion([Q0])});
            skCircle(sketch, "E60", {"center": v(-20.54, -63.93) * mm, "radius": 0.81 * mm});
            skSolve(sketch);
        }
        {
            var Q0;
            Q0 = qSketchRegion(id + "F36", true);
            var Q1;
            Q1=sQuery(id+"F33.wireOp",EDGE,"E48");
            var Q2;
            Q2=sQuery(id+"F33.wireOp",EDGE,"E50");
            var Q3;
            Q3=sQuery(id+"F33.wireOp",EDGE,"E51");
            var Q4;
            Q4=sQuery(id+"F33.wireOp",EDGE,"E52");
            var Q5;
            Q5=sQuery(id+"F33.wireOp",EDGE,"E53");
            var Q6;
            Q6=sQuery(id+"F33.wireOp",EDGE,"E54.MirrorCS");
            var Q7;
            Q7=sQuery(id+"F33.wireOp",EDGE,"E55.MirrorCS");
            var Q8;
            Q8=sQuery(id+"F33.wireOp",EDGE,"E56.MirrorCS");
            var Q9;
            Q9=sQuery(id+"F33.wireOp",EDGE,"E57.MirrorCS");
            var Q10;
            Q10=sQuery(id+"F33.wireOp",EDGE,"E58.MirrorCS");
            sweep(context, id + "F37", {"profiles" : qUnion([Q0]), "path" : qUnion([Q1, Q2, Q3, Q4, Q5, Q6, Q7, Q8, Q9, Q10])});
        }
    });
